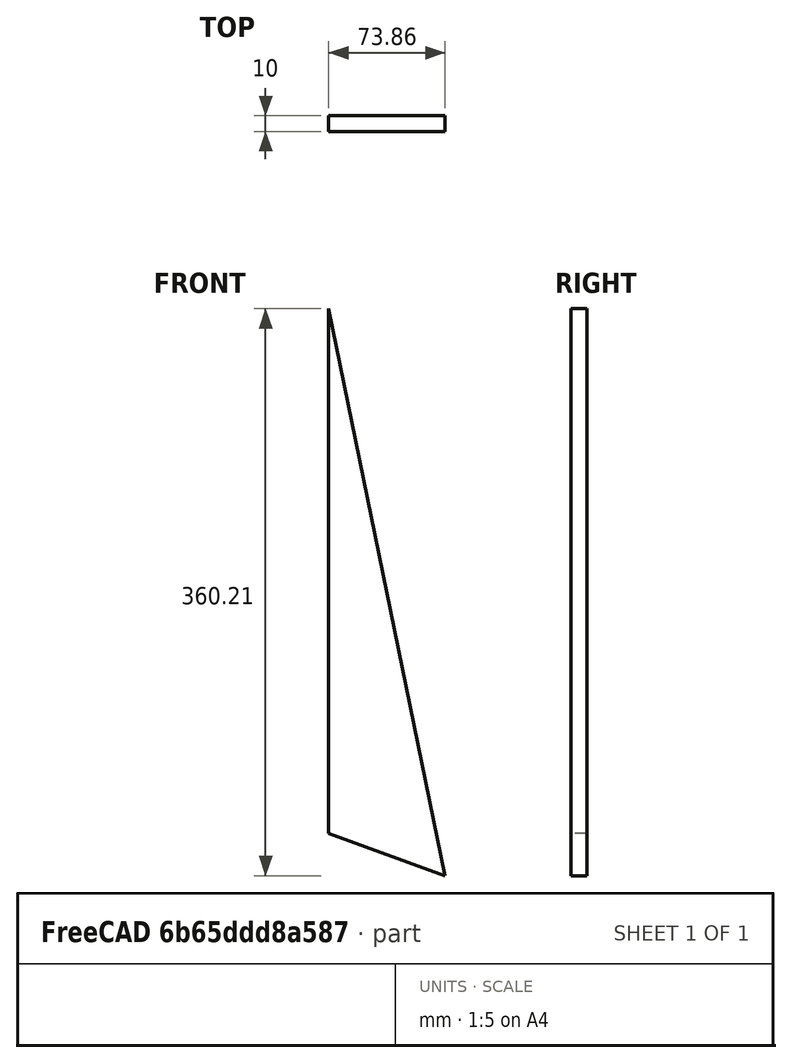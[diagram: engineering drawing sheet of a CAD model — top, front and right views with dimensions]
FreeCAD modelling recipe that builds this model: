
FCSTD DOCUMENT  (FreeCAD 0.19R24366 (Git))
Label: Tail_Boom_Support
License: All rights reserved
LicenseURL: http://en.wikipedia.org/wiki/All_rights_reserved
objects: Sketcher::SketchObject×1, PartDesign::Pad×1, Spreadsheet::Sheet×1, PartDesign::Body×1
note: 4 computed .brp shape members not serialized (recipe doc carries the construction recipe); baked Part::Feature solids carry a one-line shape summary decoded from their .brp
EXTERNAL_REF file=../../Master_of_Puppets.FCStd obj=Spreadsheet
EXTERNAL_REF file=../../Master_of_Puppets.FCStd obj=Tail

FEATURE [Sketcher::SketchObject] Sketch
  FullyConstrained = true
  MapMode = 5
  Support = -> [XY_Plane001]
  expr: Constraints[17] = Spreadsheet.SupportLength
  expr: Constraints[2] = Spreadsheet.TailBoomTriangularBraceLength
  expr: Constraints[16] = Spreadsheet.SupportWidth
  expr: Constraints[7] = Spreadsheet.TriangularAngle
  expr: Constraints[4] = Spreadsheet.TailBoomTriangularBraceWidth
  sketch-geometry (7):
    g0: LineSegment StartX=333.333 StartY=0 StartZ=0 EndX=-26.8829 EndY=-73.86 EndZ=0
    g1: LineSegment StartX=0 StartY=0 StartZ=0 EndX=333.333 EndY=0 EndZ=0
    g2: LineSegment StartX=-26.8829 StartY=-73.86 StartZ=0 EndX=0 EndY=0 EndZ=0
    g3: LineSegment StartX=-26.8829 StartY=-73.86 StartZ=0 EndX=333.333 EndY=0 EndZ=0
    g4: LineSegment StartX=-26.8829 StartY=-73.86 StartZ=0 EndX=1.14859e-11 EndY=1.64988e-11 EndZ=0
    g5: LineSegment StartX=1.14859e-11 StartY=1.64988e-11 StartZ=0 EndX=1.6e-14 EndY=0 EndZ=0
    g6: LineSegment StartX=1.6e-14 StartY=0 StartZ=0 EndX=333.333 EndY=0 EndZ=0
  constraints (18):
    c: PointOnObject(g0,g-1)
    c: Coincident(g0,g1)
    c: Distance(g1,g0) = 333.333
    c: Coincident(g2,g0)
    c: Distance(g2,g0) = 78.6002
    c: Coincident(g1,g2)
    c: Coincident(g1,g-1)
    c: Angle(g2,g1) = 1.91986
    c: Coincident(g3,g0)
    c: Coincident(g3,g0)
    c: Coincident(g4,g3)
    c: PointOnObject(g4,g2)
    c: Coincident(g5,g4)
    c: PointOnObject(g5,g1)
    c: Coincident(g6,g5)
    c: Coincident(g6,g3)
    c: Distance(g4,g3) = 78.6002
    c: Distance(g5,g3) = 333.333
FEATURE [PartDesign::Pad] Pad
  AllowMultiFace = false
  Direction = (1,1,1)
  Length = 10
  Length2 = 100
  Profile = -> Sketch
  Type = 0
  expr: Length = Spreadsheet.FlatMetalThickness
FEATURE [Spreadsheet::Sheet] Spreadsheet
  cells = A1=Inputs; A2=CalculatedWindTurbineShape; B2(CalculatedWindTurbineShape)==Master_of_Puppets#Spreadsheet.CalculatedWindTurbineShape; D2=a; E2(a)==TailBoomTriangularBraceWidth; A3=VerticalPlaneAngle; B3(VerticalPlaneAngle)==Master_of_Puppets#Spreadsheet.VerticalPlaneAngle; D3=b; E3(b)==TailBoomTriangularBraceLength; A4=FlatMetalThickness; B4(FlatMetalThickness)==Master_of_Puppets#Spreadsheet.FlatMetalThickness; D4=c; E4(c)==sqrt(a ^ 2 + b ^ 2 - 2 * a * b * cos(TriangularAngle)); F4=Law of Cosines; A5=TailBoomTriangularBraceWidth; B5(TailBoomTriangularBraceWidth)==Master_of_Puppets#Tail.TailBoomTriangularBraceWidth; D5=AngleA; E5(AngleA)==acos((a ^ 2 + c ^ 2 - b ^ 2) / (2 * a * c)); F5=Law of Cosines; A6=TailBoomTriangularBraceLength; B6(TailBoomTriangularBraceLength)==Master_of_Puppets#Tail.TailBoomTriangularBraceLength; D6=AngleB; E6(AngleB)==acos((b ^ 2 + c ^ 2 - a ^ 2) / (2 * b * c)); F6=Law of Cosines; A7=Calculated; D7=WidthOfFlatBar; E7(WidthOfFlatBar)=100; A8=TriangularAngle; B8(TriangularAngle)==90 + VerticalPlaneAngle; D8=x; E8(x)==WidthOfFlatBar / sin(AngleB); A9=Y; B9(Y)==FlatMetalThickness / 2; D9=y; E9(y)==WidthOfFlatBar / sin(AngleA); A10=SupportWidth; B10(SupportWidth)==CalculatedWindTurbineShape == <<T>> ? TailBoomTriangularBraceWidth : y; A11=SupportLength; B11(SupportLength)==CalculatedWindTurbineShape == <<T>> ? TailBoomTriangularBraceLength : x
FEATURE [PartDesign::Body] PadBody  label="Tail_Boom_Support"
  Group = -> [Sketch,Pad]
  Openafpm_Flat = true
  Origin = -> Origin001
  Placement = pos=(0,5,0) rot=(0.57735,-0.57735,0.57735;2.0944rad)
  Tip = -> Pad
  expr: .Placement.Base.y = Spreadsheet.Y
